# Revit family: Basin-Above Counter-Caroma Teo 2.0 600
name_source: partatom
category: Plumbing Fixtures
revit_build: Autodesk Revit 2014 (Build: 20140709_2115(x64)
units: mm (PartAtom-declared; Revit-internal decimal feet)

## types (1)
- Teo 2.0 600 Above Counter - 0 Tap Holes
    1 Taphole = No
    3 Tapholes = No
    Assembly Code = D2010310
    CW Connection = No
    Cost = 0 $
    Default Elevation = 0 mm  [stored 0 ft]
    Depth_ANZRS = 140 mm  [stored 0.459318 ft]
    Description = Caroma Teo 2.0 600 Above Counter Basin
    HW Connection = No
    Keynote = WB
    Length_ANZRS = 600 mm
    Manufacturer = GWA Bathrooms & Kitchens
    Material_ANZRS = Porcelain-White-Caroma
    Model = EU510100W
    ModifiedIssue_ANZRS = 20160909.01 $
    Spout Penetration = 100 mm  [stored 0.328084 ft]
    Tap Penetrations = 100 mm  [stored 0.328084 ft]
    Type Comments = Bracket included, White plug and chrome flush fitting waste included
    URL = http://specify.caroma.com.au
    Vent Connection = No
    WFU = 2
    Waste = Metal-Chrome-Caroma
    Waste Connection = Yes
    WasteOutlet_ANZRS = 0
    Width_ANZRS = 400 mm  [stored 1.31234 ft]

note: [stored X ft] marks values corroborated as IEEE doubles in the binary element streams (Revit-internal decimal feet)

## geometry (parser evidence)
native form markers: Blend x8, Sweep x1
no freeform markers — native parametric forms only
